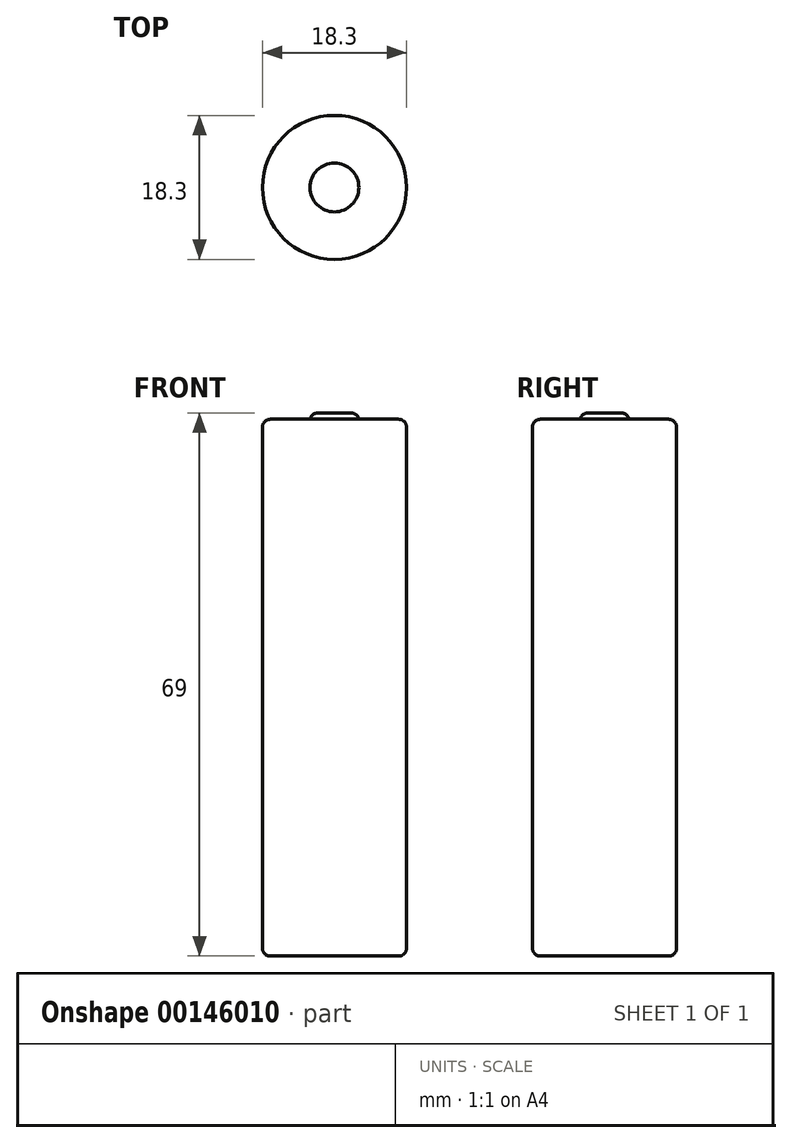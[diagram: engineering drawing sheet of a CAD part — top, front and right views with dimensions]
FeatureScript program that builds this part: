
annotation { "Feature Type Name" : "Feature", "Feature Type Description" : "" }
export const myFeature = defineFeature(function(context is Context, id is Id, definition is map)
    precondition{}
    {
        {
            var Q0;
            Q0=qCreatedBy(makeId("Top.planeOp"),FACE);
            var sketch = newSketch(context, id + "F0", { "sketchPlane" : qUnion([Q0])});
            skCircle(sketch, "E0", {"center": v(0, 0) * mm, "radius": 9.15 * mm});
            skCircle(sketch, "E1", {"center": v(0, 0) * mm, "radius": 3.1 * mm});
            skSolve(sketch);
        }
        {
            var Q0;
            Q0=makeQuery(id+"F0.imprint","IMPRINT",FACE,{"disambiguationData":[TD([[makeQuery(id+"F0.imprint","IMPRINT",EDGE,{"derivedFrom":sQuery(id+"F0.wireOp",EDGE,"E0")}),1.0]])]});
            extrude(context, id + "F1", {"entities" : qUnion([Q0]), "depth" : 68.2 * mm});
        }
        {
            var Q0;
            Q0=makeQuery(id+"F0.imprint","IMPRINT",FACE,{"disambiguationData":[TD([[makeQuery(id+"F0.imprint","IMPRINT",EDGE,{"derivedFrom":sQuery(id+"F0.wireOp",EDGE,"E1")}),1.0]])]});
            var Q1;
            Q1=sQuery(id+"F0.wireOp",EDGE,"E1");
            extrude(context, id + "F2", {"entities" : qUnion([Q0]), "operationType" : NewBodyOperationType.ADD, "surfaceEntities" : qUnion([Q1]), "depth" : 69 * mm});
        }
        {
            var Q0;
            Q0=makeQuery(id+"F2.opExtrude","CAP_EDGE",EDGE,{"disambiguationData":[OSD([sQuery(id+"F0.wireOp",EDGE,"E1")])],"isStart":false});
            var Q1;
            Q1=makeQuery(id+"F1.opExtrude","CAP_EDGE",EDGE,{"disambiguationData":[OSD([sQuery(id+"F0.wireOp",EDGE,"E0")])],"isStart":false});
            var Q2;
            Q2=makeQuery(id+"F1.opExtrude","CAP_EDGE",EDGE,{"disambiguationData":[OSD([sQuery(id+"F0.wireOp",EDGE,"E0")])],"isStart":true});
            fillet(context, id + "F3", {"entities" : qUnion([Q0, Q1, Q2]), "radius" : 1 * mm, "tangentPropagation" : true, "allowEdgeOverflow" : false});
        }
    });
